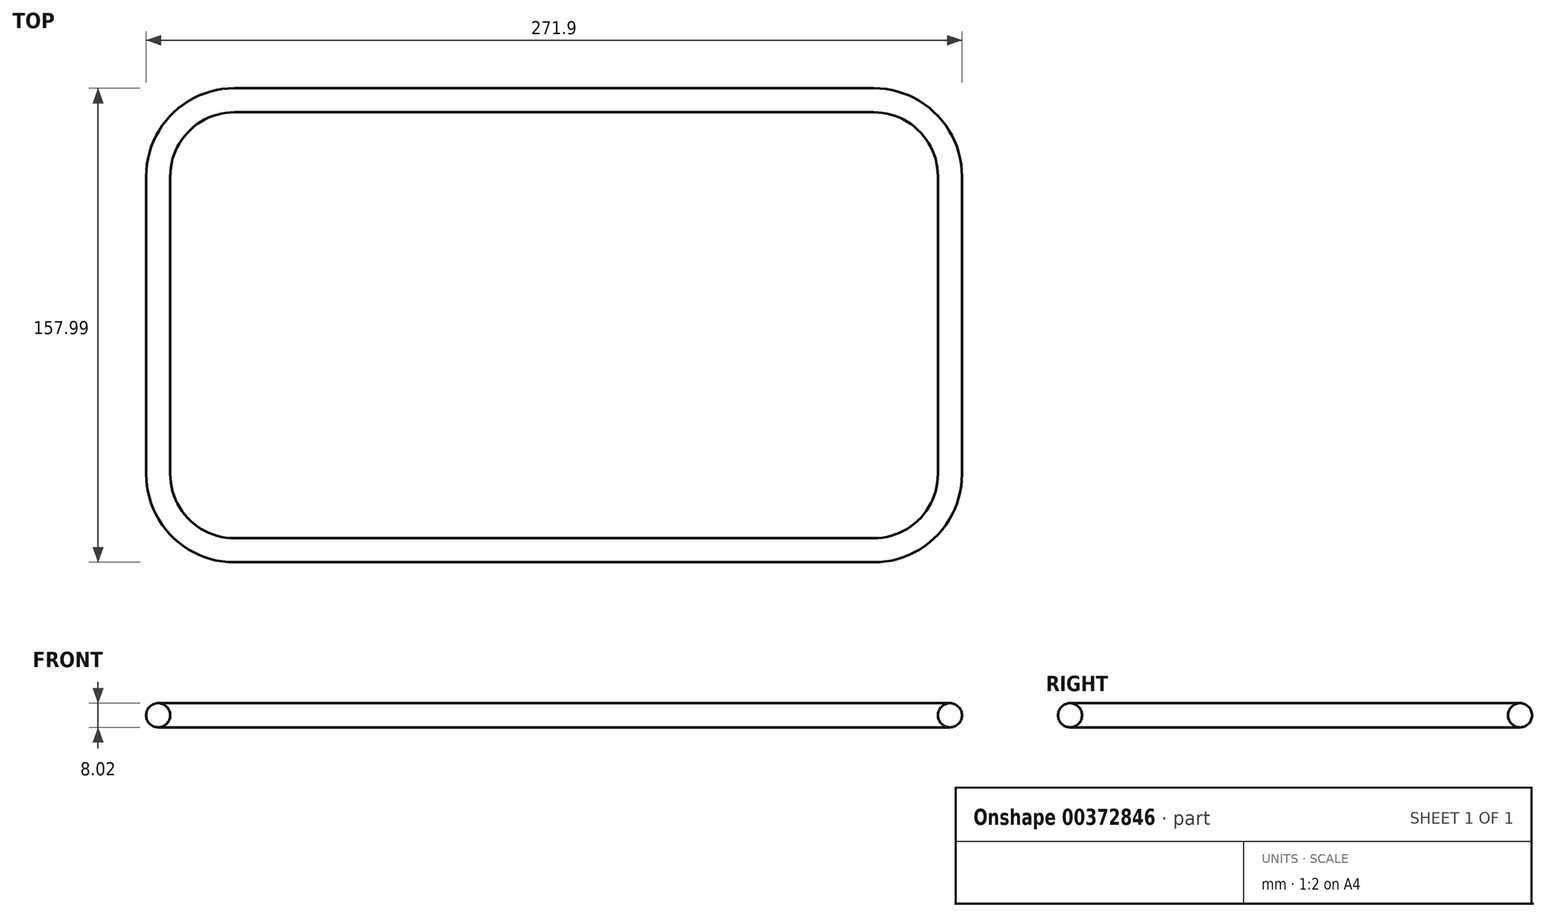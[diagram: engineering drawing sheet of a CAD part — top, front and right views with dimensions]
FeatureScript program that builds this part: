
annotation { "Feature Type Name" : "Feature", "Feature Type Description" : "" }
export const myFeature = defineFeature(function(context is Context, id is Id, definition is map)
    precondition{}
    {
        {
            var Q0;
            Q0=qCreatedBy(makeId("Top.planeOp"),FACE);
            var sketch = newSketch(context, id + "F0", { "sketchPlane" : qUnion([Q0])});
            skLineSegment(sketch, "E0.bottom", {"start": v(-100.73, 82.05) * mm, "end": v(112.35, 82.05) * mm});
            skLineSegment(sketch, "E0.top", {"start": v(-100.73, -67.92) * mm, "end": v(112.35, -67.92) * mm});
            skLineSegment(sketch, "E0.left", {"start": v(-126.13, 56.65) * mm, "end": v(-126.13, -42.52) * mm});
            skLineSegment(sketch, "E0.right", {"start": v(137.75, 56.65) * mm, "end": v(137.75, -42.52) * mm});
            skPoint(sketch, "E1.oppositeSnap0", {"position": v(5.81, 82.05) * mm});
            skPoint(sketch, "E2.visualSharp", {"position": v(-126.13, 82.05) * mm});
            skArc(sketch, "E2.filletArc", {"start": v(-100.73, 82.05) * mm, "mid": v(-118.7, 74.6) * mm, "end": v(-126.13, 56.65) * mm});
            skPoint(sketch, "E3.visualSharp", {"position": v(137.75, 82.05) * mm});
            skArc(sketch, "E3.filletArc", {"start": v(137.75, 56.65) * mm, "mid": v(130.31, 74.6) * mm, "end": v(112.35, 82.05) * mm});
            skPoint(sketch, "E4.visualSharp", {"position": v(137.75, -67.92) * mm});
            skArc(sketch, "E4.filletArc", {"start": v(112.35, -67.92) * mm, "mid": v(130.31, -60.48) * mm, "end": v(137.75, -42.52) * mm});
            skPoint(sketch, "E5.visualSharp", {"position": v(-126.13, -67.92) * mm});
            skArc(sketch, "E5.filletArc", {"start": v(-126.13, -42.52) * mm, "mid": v(-118.7, -60.48) * mm, "end": v(-100.73, -67.92) * mm});
            skSolve(sketch);
        }
        {
            var Q0;
            Q0=qCreatedBy(makeId("Right.planeOp"),FACE);
            var sketch = newSketch(context, id + "F1", { "sketchPlane" : qUnion([Q0])});
            skLineSegment(sketch, "E6.0", {"start": v(56.65, 0) * mm, "end": v(-42.52, 0) * mm});
            skLineSegment(sketch, "E6.1", {"start": v(-42.52, 0) * mm, "end": v(-67.92, 0) * mm});
            skLineSegment(sketch, "E6.2", {"start": v(56.65, 0) * mm, "end": v(82.05, 0) * mm});
            skLineSegment(sketch, "E6.3", {"start": v(82.05, 0) * mm, "end": v(56.65, 0) * mm});
            skLineSegment(sketch, "E6.4", {"start": v(-67.92, 0) * mm, "end": v(-42.52, 0) * mm});
            skLineSegment(sketch, "E6.5", {"start": v(56.65, 0) * mm, "end": v(-42.52, 0) * mm});
            skCircle(sketch, "E7", {"center": v(82.05, 0) * mm, "radius": 4.01 * mm});
            skSolve(sketch);
        }
        {
            var Q0;
            Q0=makeQuery(id+"F1.imprint","IMPRINT",FACE,{"disambiguationData":[TD([[makeQuery(id+"F1.imprint","IMPRINT",EDGE,{"derivedFrom":sQuery(id+"F1.wireOp",EDGE,"E7")}),1.0]])]});
            var Q1;
            Q1=sQuery(id+"F0.wireOp",EDGE,"E0.right");
            var Q2;
            Q2=sQuery(id+"F0.wireOp",EDGE,"E4.filletArc");
            var Q3;
            Q3=sQuery(id+"F0.wireOp",EDGE,"E0.top");
            var Q4;
            Q4=sQuery(id+"F0.wireOp",EDGE,"E5.filletArc");
            var Q5;
            Q5=sQuery(id+"F0.wireOp",EDGE,"E0.left");
            var Q6;
            Q6=sQuery(id+"F0.wireOp",EDGE,"E2.filletArc");
            var Q7;
            Q7=sQuery(id+"F0.wireOp",EDGE,"E0.bottom");
            var Q8;
            Q8=sQuery(id+"F0.wireOp",EDGE,"E3.filletArc");
            sweep(context, id + "F2", {"profiles" : qUnion([Q0]), "path" : qUnion([Q1, Q2, Q3, Q4, Q5, Q6, Q7, Q8])});
        }
    });
